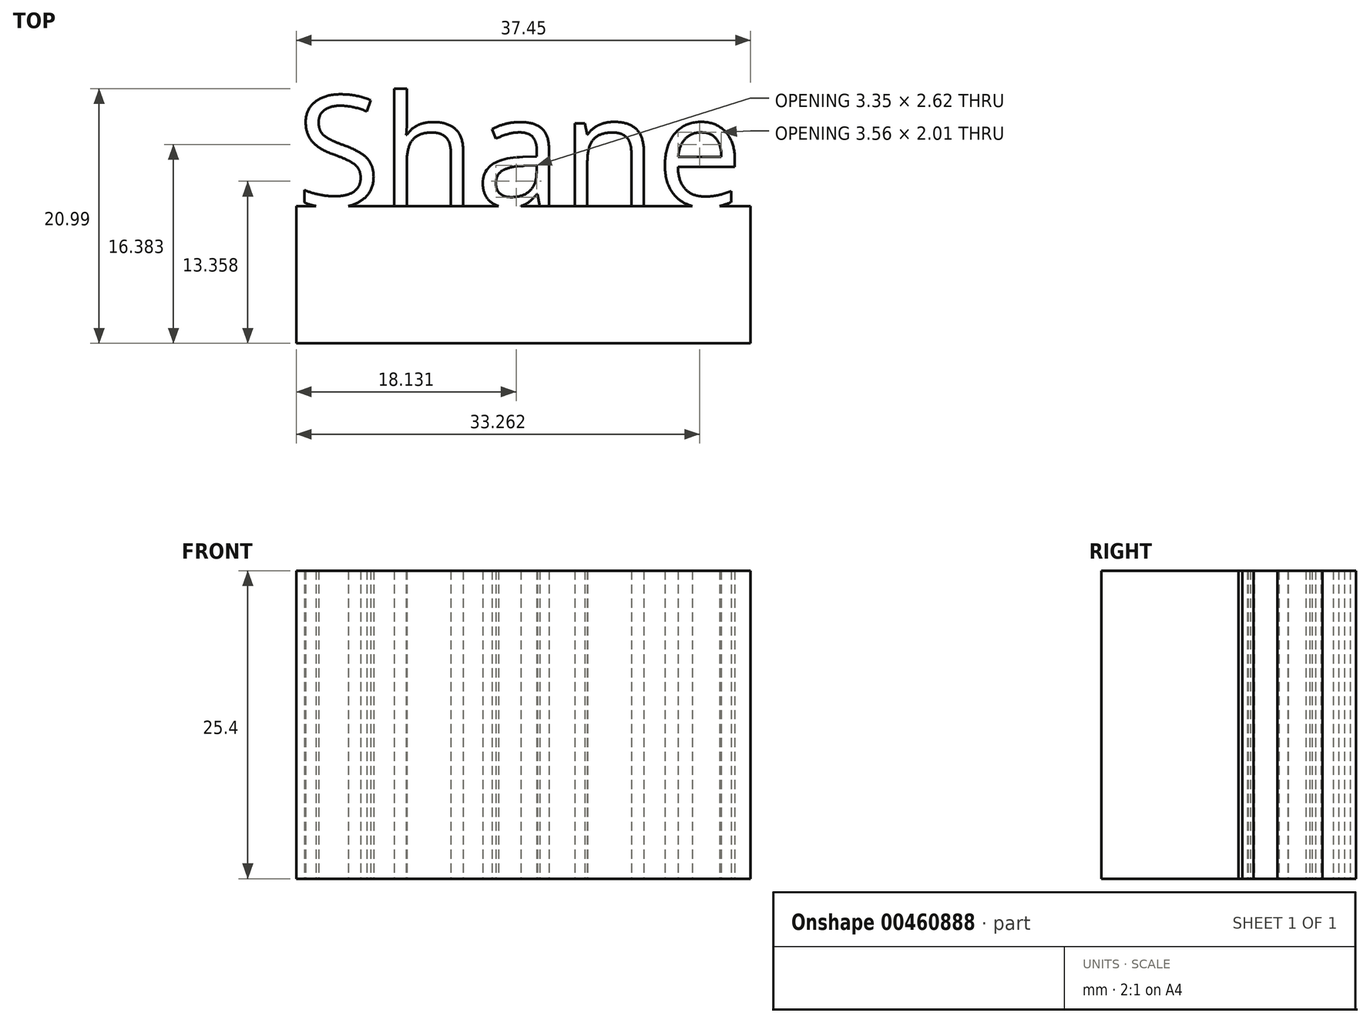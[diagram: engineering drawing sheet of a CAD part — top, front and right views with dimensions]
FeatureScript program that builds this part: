
annotation { "Feature Type Name" : "Feature", "Feature Type Description" : "" }
export const myFeature = defineFeature(function(context is Context, id is Id, definition is map)
    precondition{}
    {
        {
            var Q0;
            Q0=qCreatedBy(makeId("Top.planeOp"),FACE);
            var sketch = newSketch(context, id + "F0", { "sketchPlane" : qUnion([Q0])});
            skText(sketch, "E0", { "text": "Shane", "fontName": "OpenSans-Regular.ttf"});
            skLineSegment(sketch, "E1.bottom", {"start": v(-54.15, 50.65) * mm, "end": v(-16.7, 50.65) * mm});
            skLineSegment(sketch, "E1.top", {"start": v(-54.15, 39.33) * mm, "end": v(-16.7, 39.33) * mm});
            skLineSegment(sketch, "E1.left", {"start": v(-54.15, 50.65) * mm, "end": v(-54.15, 39.33) * mm});
            skLineSegment(sketch, "E1.right", {"start": v(-16.7, 50.65) * mm, "end": v(-16.7, 39.33) * mm});
            const initialGuessF0  = {"E0": [-0.05415, 0.05065, 1, 0, 0.00916]};
            skSetInitialGuess(sketch, initialGuessF0);
            skSolve(sketch);
        }
        {
            var Q0;
            Q0 = qSketchRegion(id + "F0", true);
            extrude(context, id + "F1", {"entities" : qUnion([Q0]), "depth" : 25.4 * mm});
        }
    });
